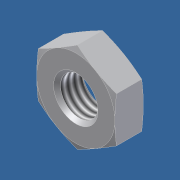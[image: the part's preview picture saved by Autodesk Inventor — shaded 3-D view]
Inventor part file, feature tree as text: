
AUTODESK INVENTOR PART (.ipt)
format: ipt  version: 2012 (Build 160160000, 160)  size: 128,000 bytes
history: native  units: in
note: dims shown in document units (in); Inventor stores cm internally (conversion verified against a paired STEP export)
features: other x70, sketch x3, revolve x2, extrude x1, thread x1
ambient origin geometry x8: Origin, YZ Plane, XZ Plane, XY Plane, X Axis, Y Axis, Z Axis, Center Point
bodies: Solid1 (feature_tree)
feature tree (77):
  sketch  "Sketch_8"  dims[d0=360.0deg d1=0.16in d2=0.0in]
  sketch  "Sketch_10"  dims[d3=360.0deg d4=0.16in d5=0.0in]
  revolve  "Revolution1"  [1 undecoded]
  extrude  "Extrusion1"  Depth=0.16in TaperAngle=0.0deg
  revolve  "Revolution2"  [1 undecoded]
  thread  "Thread1"  [1 undecoded]
  other  "NUT_XY"
  other  "NUT_YZ"
  other  "NUT_ZX"
  other  "NUT_X"
  other  "NUT_Y"
  other  "NUT_Z"
  other  "NUT_Center"
  other  "a1_XY"
  other  "a1_YZ"
  other  "a1_ZX"
  other  "a1_X"
  other  "a1_Y"
  other  "a1_Z"
  other  "a1_Center"
  other  "a2_XY"
  other  "a2_YZ"
  other  "a2_ZX"
  other  "a2_X"
  other  "a2_Y"
  other  "a2_Z"
  other  "a2_Center"
  other  "b1_XY"
  other  "b1_YZ"
  other  "b1_ZX"
  other  "b1_X"
  other  "b1_Y"
  other  "b1_Z"
  other  "b1_Center"
  other  "b2_XY"
  other  "b2_YZ"
  other  "b2_ZX"
  other  "b2_X"
  other  "b2_Y"
  other  "b2_Z"
  other  "b2_Center"
  other  "e_XY"
  other  "e_YZ"
  other  "e_ZX"
  other  "e_X"
  other  "e_Y"
  other  "e_Z"
  other  "e_Center"
  other  "th1_XY"
  other  "th1_YZ"
  other  "th1_ZX"
  other  "th1_X"
  other  "th1_Y"
  other  "th1_Z"
  other  "th1_Center"
  other  "th2_XY"
  other  "th2_YZ"
  other  "th2_ZX"
  other  "th2_X"
  other  "th2_Y"
  other  "th2_Z"
  other  "th2_Center"
  other  "ol1_XY"
  other  "ol1_YZ"
  other  "ol1_ZX"
  other  "ol1_X"
  other  "ol1_Y"
  other  "ol1_Z"
  other  "ol1_Center"
  other  "ol2_XY"
  other  "ol2_YZ"
  other  "ol2_ZX"
  other  "ol2_X"
  other  "ol2_Y"
  other  "ol2_Z"
  other  "ol2_Center"
  sketch  "Sketch_11"
note: 3 required parameter values undecoded (feature->parameter linkage not recoverable at this tier; creation-order binding heuristic only, values carry confidence <= 0.55)